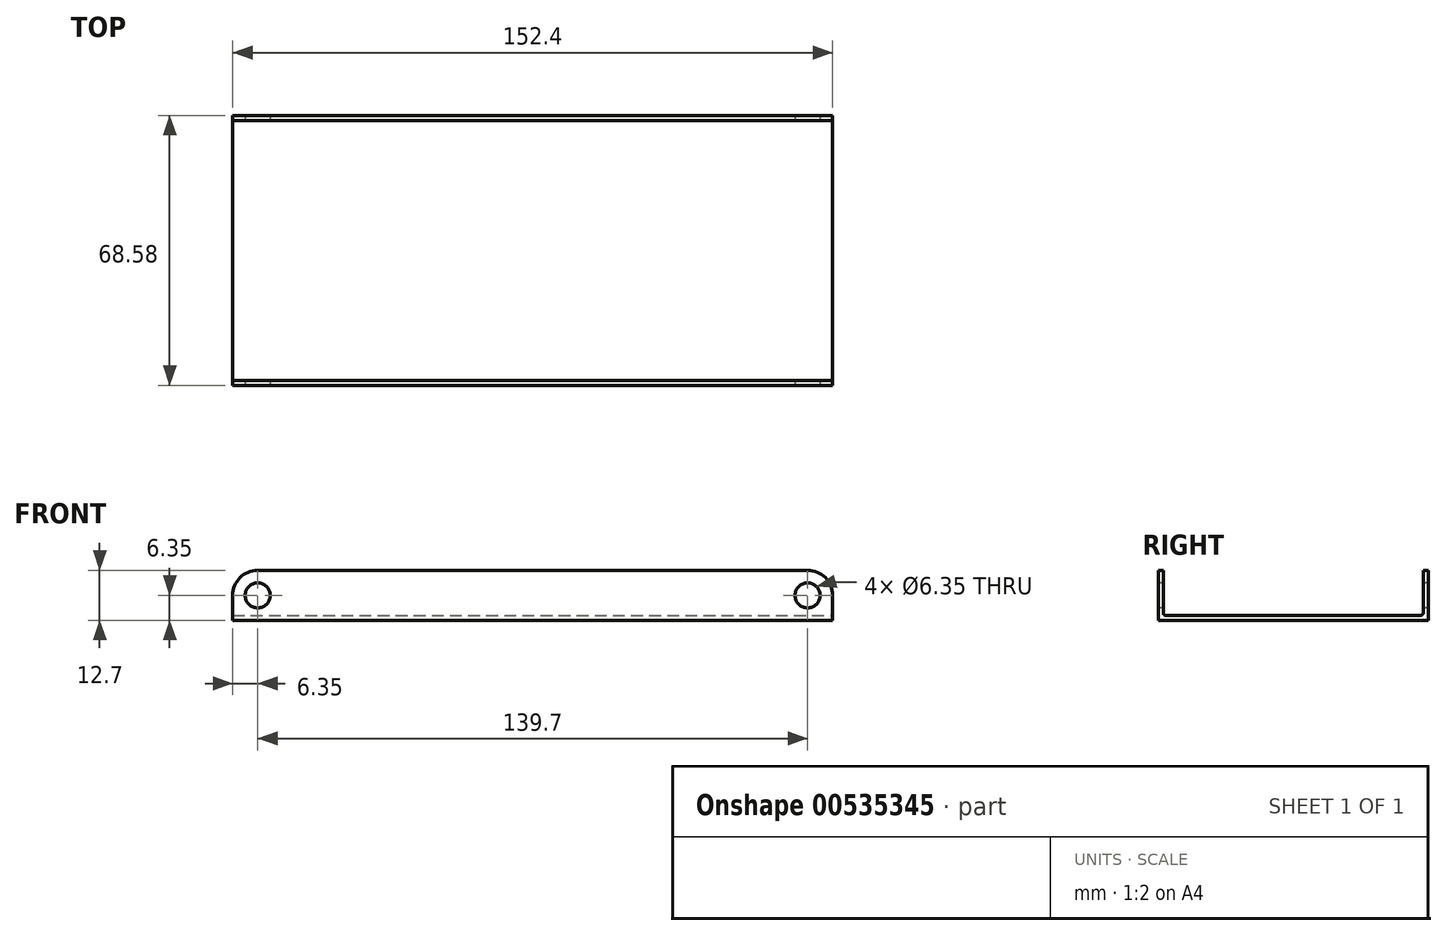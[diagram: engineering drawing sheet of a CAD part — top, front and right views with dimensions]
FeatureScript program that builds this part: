
annotation { "Feature Type Name" : "Feature", "Feature Type Description" : "" }
export const myFeature = defineFeature(function(context is Context, id is Id, definition is map)
    precondition{}
    {
        {
            var Q0;
            Q0=qCreatedBy(makeId("Front.planeOp"),FACE);
            var sketch = newSketch(context, id + "F0", { "sketchPlane" : qUnion([Q0])});
            skLineSegment(sketch, "E0.bottom", {"start": v(0, 0) * mm, "end": v(-152.4, 0) * mm});
            skLineSegment(sketch, "E0.top", {"start": v(-6.35, 12.7) * mm, "end": v(-146.05, 12.7) * mm});
            skLineSegment(sketch, "E0.left", {"start": v(0, 0) * mm, "end": v(0, 6.35) * mm});
            skLineSegment(sketch, "E0.right", {"start": v(-152.4, 0) * mm, "end": v(-152.4, 6.35) * mm});
            skPoint(sketch, "E1.visualSharp", {"position": v(-152.4, 12.7) * mm});
            skArc(sketch, "E1.filletArc", {"start": v(-146.05, 12.7) * mm, "mid": v(-150.54, 10.84) * mm, "end": v(-152.4, 6.35) * mm});
            skPoint(sketch, "E2.visualSharp", {"position": v(0, 12.7) * mm});
            skArc(sketch, "E2.filletArc", {"start": v(0, 6.35) * mm, "mid": v(-1.86, 10.84) * mm, "end": v(-6.35, 12.7) * mm});
            skLineSegment(sketch, "E3", {"start": v(-146.05, 6.35) * mm, "end": v(-6.35, 6.35) * mm, "construction": true});
            skCircle(sketch, "E4", {"center": v(-146.05, 6.35) * mm, "radius": 3.17 * mm});
            skCircle(sketch, "E5", {"center": v(-6.35, 6.35) * mm, "radius": 3.17 * mm});
            skSolve(sketch);
        }
        {
            var Q0;
            Q0 = qSketchRegion(id + "F0", true);
            extrude(context, id + "F1", {"entities" : qUnion([Q0]), "oppositeDirection" : true, "depth" : 68.58 * mm, "offsetDistance" : 25.4 * mm});
        }
        {
            var Q0;
            Q0=qCreatedBy(makeId("Right.planeOp"),FACE);
            var sketch = newSketch(context, id + "F2", { "sketchPlane" : qUnion([Q0])});
            skLineSegment(sketch, "E6.0.0", {"start": v(0, 12.7) * mm, "end": v(0, 6.35) * mm, "construction": true});
            skLineSegment(sketch, "E6.0.1", {"start": v(0, 6.35) * mm, "end": v(68.58, 6.35) * mm, "construction": true});
            skLineSegment(sketch, "E6.0.2", {"start": v(68.58, 6.35) * mm, "end": v(68.58, 12.7) * mm, "construction": true});
            skLineSegment(sketch, "E6.0.3", {"start": v(68.58, 12.7) * mm, "end": v(0, 12.7) * mm, "construction": true});
            skLineSegment(sketch, "E7.0.0", {"start": v(0, 6.35) * mm, "end": v(0, 0) * mm, "construction": true});
            skLineSegment(sketch, "E7.0.1", {"start": v(0, 0) * mm, "end": v(68.58, 0) * mm, "construction": true});
            skLineSegment(sketch, "E7.0.2", {"start": v(68.58, 0) * mm, "end": v(68.58, 6.35) * mm, "construction": true});
            skLineSegment(sketch, "E7.0.3", {"start": v(68.58, 6.35) * mm, "end": v(0, 6.35) * mm, "construction": true});
            skLineSegment(sketch, "E8.bottom", {"start": v(1.27, 61.32) * mm, "end": v(67.31, 61.32) * mm});
            skLineSegment(sketch, "E8.top", {"start": v(1.9, 1.27) * mm, "end": v(66.68, 1.27) * mm});
            skLineSegment(sketch, "E8.left", {"start": v(1.27, 61.32) * mm, "end": v(1.27, 1.9) * mm});
            skLineSegment(sketch, "E8.right", {"start": v(67.31, 61.32) * mm, "end": v(67.31, 1.9) * mm});
            skLineSegment(sketch, "E9", {"start": v(1.27, 1.27) * mm, "end": v(0, 1.27) * mm, "construction": true});
            skLineSegment(sketch, "E10", {"start": v(67.31, 1.27) * mm, "end": v(68.58, 1.27) * mm, "construction": true});
            skLineSegment(sketch, "E11", {"start": v(67.31, 1.27) * mm, "end": v(67.31, 0) * mm, "construction": true});
            skPoint(sketch, "E12.visualSharp", {"position": v(67.31, 1.27) * mm});
            skArc(sketch, "E12.filletArc", {"start": v(66.68, 1.27) * mm, "mid": v(67.12, 1.46) * mm, "end": v(67.31, 1.9) * mm});
            skPoint(sketch, "E13.visualSharp", {"position": v(1.27, 1.27) * mm});
            skArc(sketch, "E13.filletArc", {"start": v(1.27, 1.9) * mm, "mid": v(1.46, 1.46) * mm, "end": v(1.9, 1.27) * mm});
            skPoint(sketch, "E14", {"position": v(34.3, 1.27) * mm});
            skSolve(sketch);
        }
        {
            var Q0;
            Q0 = qSketchRegion(id + "F2", true);
            extrude(context, id + "F3", {"entities" : qUnion([Q0]), "operationType" : NewBodyOperationType.REMOVE, "endBound" : BoundingType.THROUGH_ALL, "oppositeDirection" : true, "depth" : 25.4 * mm, "offsetDistance" : 25.4 * mm});
        }
    });
